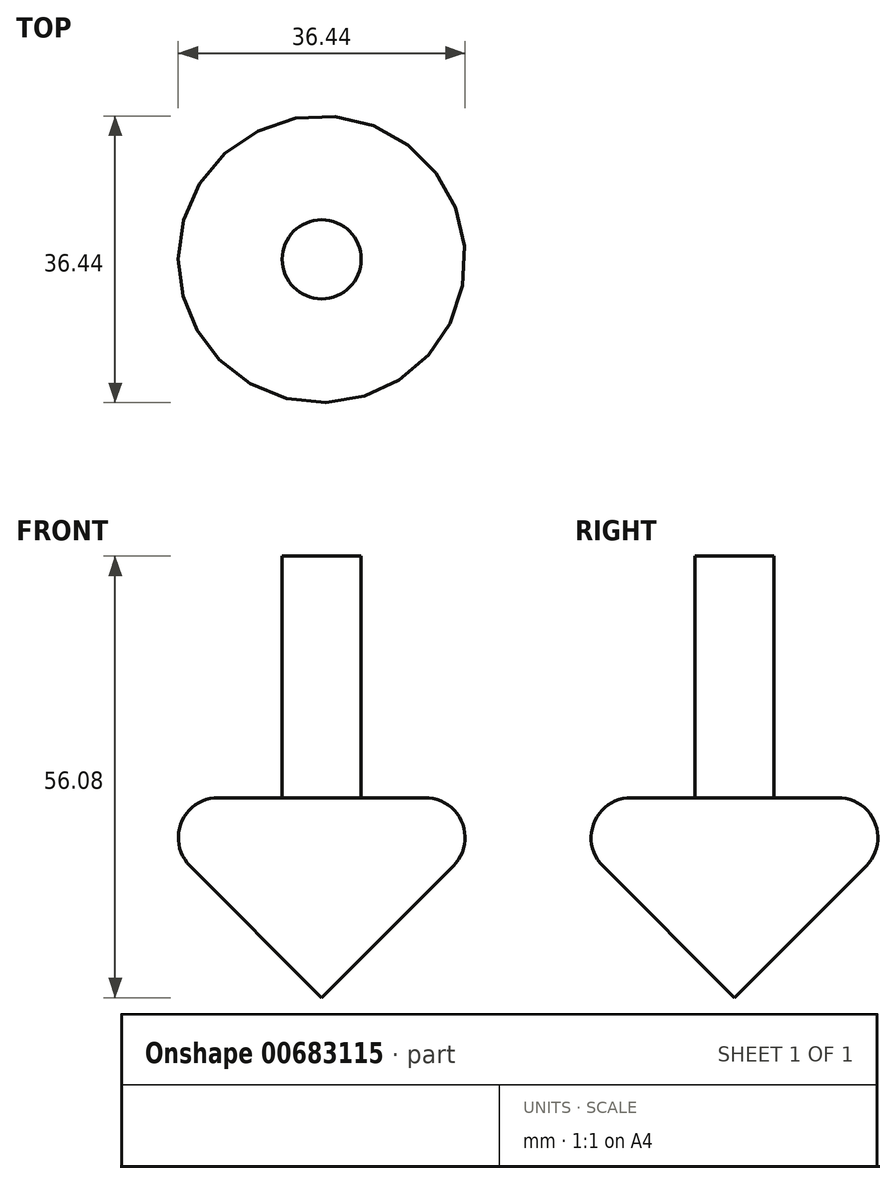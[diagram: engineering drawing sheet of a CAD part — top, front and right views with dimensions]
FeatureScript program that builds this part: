
annotation { "Feature Type Name" : "Feature", "Feature Type Description" : "" }
export const myFeature = defineFeature(function(context is Context, id is Id, definition is map)
    precondition{}
    {
        {
            var Q0;
            Q0=qCreatedBy(makeId("Front.planeOp"),FACE);
            var sketch = newSketch(context, id + "F0", { "sketchPlane" : qUnion([Q0])});
            skLineSegment(sketch, "E0", {"start": v(0, 0) * mm, "end": v(0, -25.4) * mm});
            skLineSegment(sketch, "E1", {"start": v(0, 0) * mm, "end": v(-25.4, 0) * mm});
            skLineSegment(sketch, "E2", {"start": v(-25.4, 0) * mm, "end": v(0, -25.4) * mm});
            skLineSegment(sketch, "E3", {"start": v(0, 0) * mm, "end": v(0, 50.8) * mm});
            skLineSegment(sketch, "E4", {"start": v(0, 50.8) * mm, "end": v(-5.02, 50.8) * mm});
            skLineSegment(sketch, "E5", {"start": v(-5.02, 50.8) * mm, "end": v(-5.02, 0) * mm});
            skSolve(sketch);
        }
        {
            var Q0;
            Q0 = qSketchRegion(id + "F0", true);
            var Q1;
            Q1=sQuery(id+"F0.wireOp",EDGE,"E3");
            revolve(context, id + "F1", {"entities" : qUnion([Q0]), "axis" : qUnion([Q1]), "revolveType" : RevolveType.FULL});
        }
        {
            var Q0;
            Q0=makeQuery(id+"F1.opRevolve","SWEPT_EDGE",EDGE,{"disambiguationData":[OSD([sQuery(id+"F0.wireOp",EDGE,"E1"),sQuery(id+"F0.wireOp",EDGE,"E2")])]});
            fillet(context, id + "F2", {"entities" : qUnion([Q0]), "radius" : 5.08 * mm, "tangentPropagation" : true, "allowEdgeOverflow" : false});
        }
        {
            var Q0;
            Q0=qCreatedBy(makeId("Top.planeOp"),FACE);
            cPlane(context, id + "F3", {"entities" : qUnion([Q0]), "cplaneType" : CPlaneType.OFFSET, "offset" : 52.33 * mm, "width" : 152.4 * mm, "height" : 152.4 * mm});
        }
        {
            var Q0;
            Q0=qCreatedBy(id+"F3.planeOp",FACE);
            var sketch = newSketch(context, id + "F4", { "sketchPlane" : qUnion([Q0])});
            skLineSegment(sketch, "E6.bottom", {"start": v(-28.77, 73.1) * mm, "end": v(45.82, 73.1) * mm});
            skLineSegment(sketch, "E6.top", {"start": v(-28.77, -41.24) * mm, "end": v(45.82, -41.24) * mm});
            skLineSegment(sketch, "E6.left", {"start": v(-28.77, 73.1) * mm, "end": v(-28.77, -41.24) * mm});
            skLineSegment(sketch, "E6.right", {"start": v(45.82, 73.1) * mm, "end": v(45.82, -41.24) * mm});
            skSolve(sketch);
        }
        {
            var Q0;
            Q0 = qSketchRegion(id + "F4", true);
            extrude(context, id + "F5", {"entities" : qUnion([Q0]), "operationType" : NewBodyOperationType.REMOVE, "oppositeDirection" : true, "depth" : 21.65 * mm, "offsetDistance" : 25.4 * mm});
        }
    });
